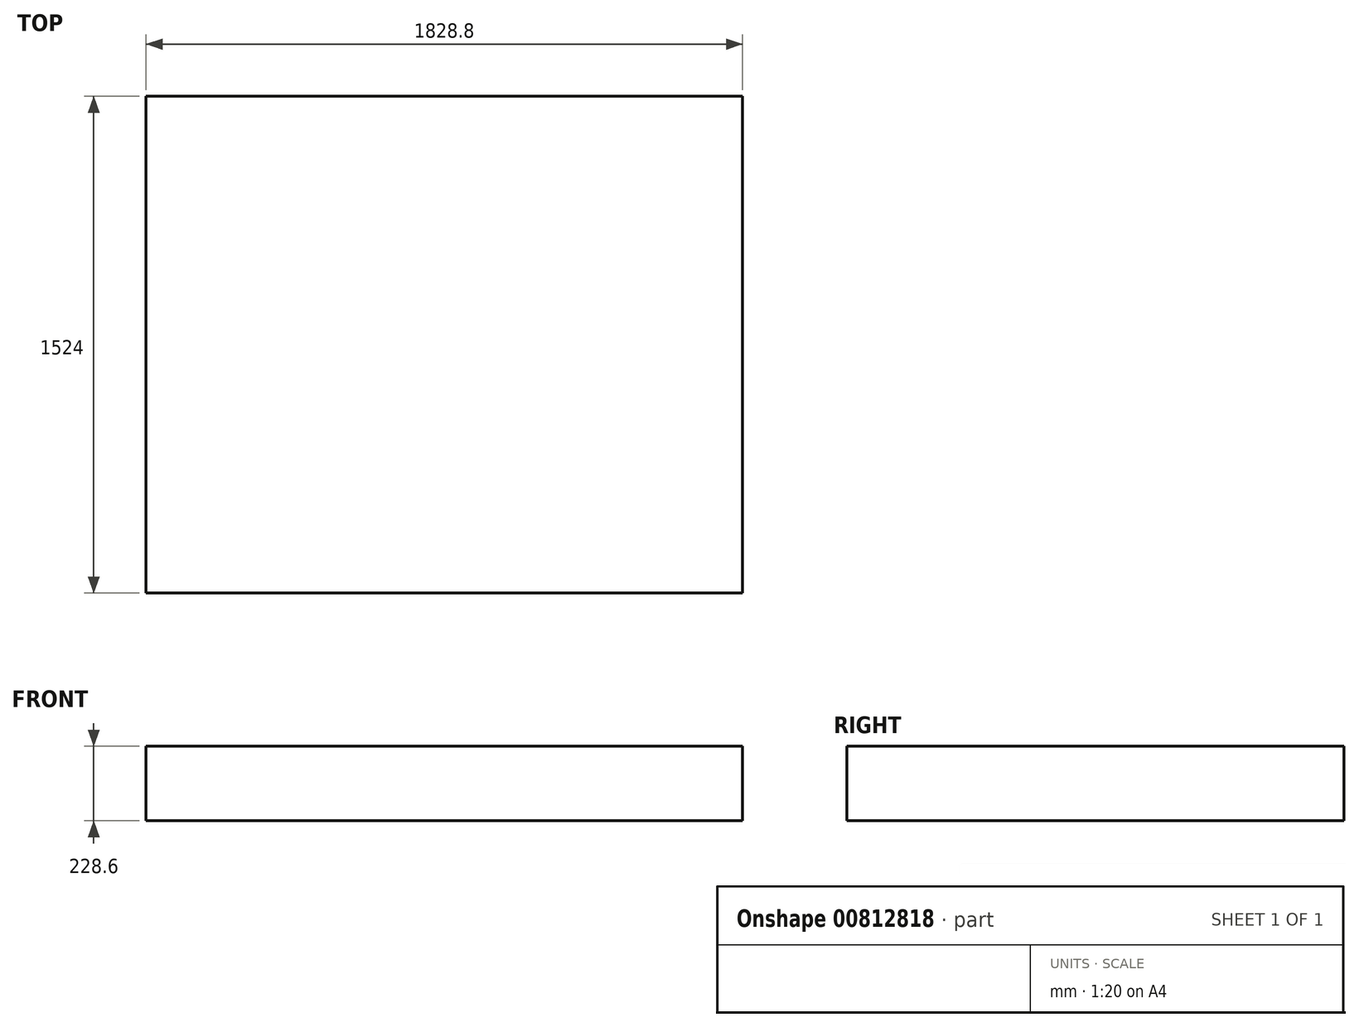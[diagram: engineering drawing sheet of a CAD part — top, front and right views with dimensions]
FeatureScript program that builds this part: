
annotation { "Feature Type Name" : "Feature", "Feature Type Description" : "" }
export const myFeature = defineFeature(function(context is Context, id is Id, definition is map)
    precondition{}
    {
        {
            var Q0;
            Q0=qCreatedBy(makeId("Top.planeOp"),FACE);
            var sketch = newSketch(context, id + "F0", { "sketchPlane" : qUnion([Q0])});
            skLineSegment(sketch, "E0", {"start": v(-3039.17, 2049.38) * mm, "end": v(6104.83, 2049.38) * mm});
            skLineSegment(sketch, "E1", {"start": v(-3039.17, 2049.38) * mm, "end": v(-3039.17, 5097.38) * mm});
            skLineSegment(sketch, "E2", {"start": v(-3039.17, 2049.38) * mm, "end": v(-3039.17, -1608.22) * mm, "construction": true});
            skLineSegment(sketch, "E3", {"start": v(-3039.17, -1608.22) * mm, "end": v(8.83, -1608.22) * mm, "construction": true});
            skLineSegment(sketch, "E4", {"start": v(8.83, -1608.22) * mm, "end": v(1837.63, -1608.22) * mm, "construction": true});
            skLineSegment(sketch, "E5", {"start": v(1837.63, -1608.22) * mm, "end": v(5495.23, -1608.22) * mm, "construction": true});
            skLineSegment(sketch, "E6", {"start": v(8.83, 2049.38) * mm, "end": v(8.83, 525.38) * mm});
            skLineSegment(sketch, "E7", {"start": v(8.83, 525.38) * mm, "end": v(1837.63, 525.38) * mm});
            skLineSegment(sketch, "E8", {"start": v(1837.63, 525.38) * mm, "end": v(1837.63, 2049.38) * mm});
            skLineSegment(sketch, "E9", {"start": v(8.83, 525.38) * mm, "end": v(8.83, -1608.22) * mm});
            skLineSegment(sketch, "E10", {"start": v(1837.63, -1608.22) * mm, "end": v(1837.63, 525.38) * mm});
            skText(sketch, "E11", { "text": "Building", "fontName": "OpenSans-Regular.ttf"});
            skLineSegment(sketch, "E12.bottom", {"start": v(1837.63, 2049.38) * mm, "end": v(5495.23, 2049.38) * mm});
            skLineSegment(sketch, "E12.top", {"start": v(1837.63, -1608.22) * mm, "end": v(5495.23, -1608.22) * mm});
            skLineSegment(sketch, "E12.left", {"start": v(1837.63, 2049.38) * mm, "end": v(1837.63, -1608.22) * mm});
            skLineSegment(sketch, "E12.right", {"start": v(5495.23, 2049.38) * mm, "end": v(5495.23, -1608.22) * mm});
            const initialGuessF0  = {"E11": [-1.91007, 3.32846, 1, 0, 0.60026]};
            skSetInitialGuess(sketch, initialGuessF0);
            skSolve(sketch);
        }
        {
            var Q0;
            {var subQ0=sQuery(id+"F0.wireOp",EDGE,"E6");Q0=makeQuery(id+"F0.imprint","IMPRINT",FACE,{"disambiguationData":[TD([[makeQuery(id+"F0.imprint","IMPRINT",EDGE,{"derivedFrom":subQ0}),1.0]])]});}
            var Q1;
            {var subQ3=sQuery(id+"F0.wireOp",EDGE,"E12.bottom");Q1=makeQuery(id+"F0.imprint","IMPRINT",FACE,{"disambiguationData":[TD([[makeQuery(id+"F0.imprint","IMPRINT",EDGE,{"derivedFrom":subQ3}),-1.0]])]});}
            extrude(context, id + "F1", {"entities" : qUnion([Q0, Q1]), "oppositeDirection" : true, "depth" : 228.6 * mm, "offsetDistance" : 30.48 * mm});
        }
    });
